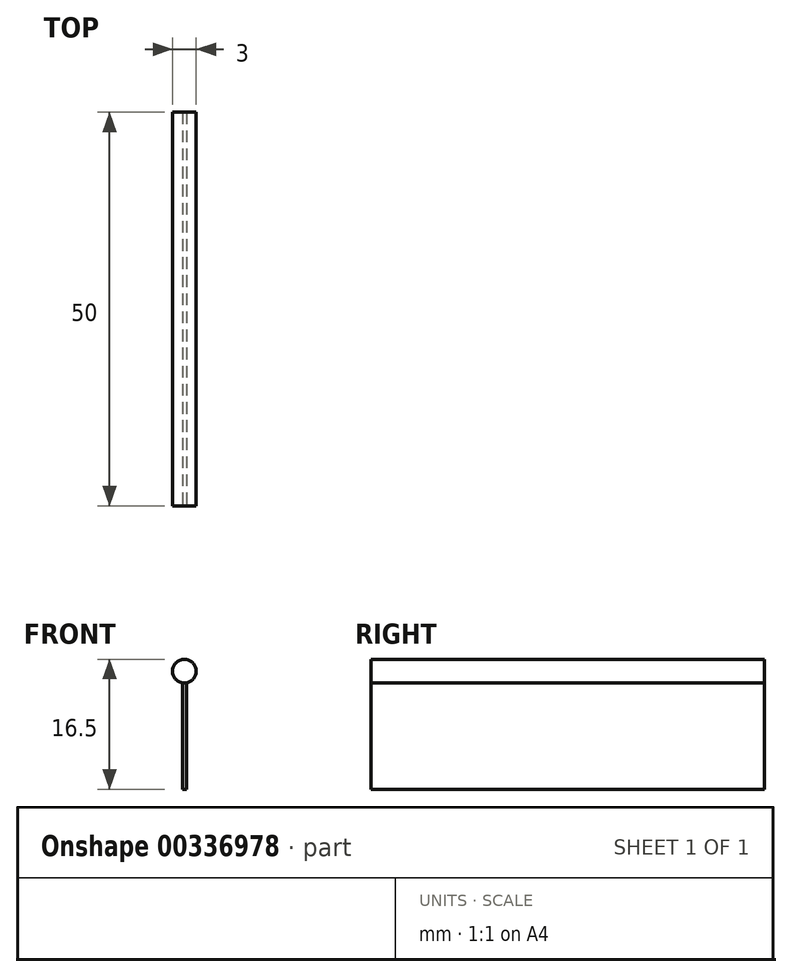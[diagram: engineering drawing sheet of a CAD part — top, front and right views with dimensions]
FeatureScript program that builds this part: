
annotation { "Feature Type Name" : "Feature", "Feature Type Description" : "" }
export const myFeature = defineFeature(function(context is Context, id is Id, definition is map)
    precondition{}
    {
        {
            var Q0;
            Q0=qCreatedBy(makeId("Front.planeOp"),FACE);
            var sketch = newSketch(context, id + "F0", { "sketchPlane" : qUnion([Q0])});
            skCircle(sketch, "E0", {"center": v(0, 35.6) * mm, "radius": 1.5 * mm});
            skPoint(sketch, "E1.start.orphan", {"position": v(-0.25, 35.6) * mm});
            skSolve(sketch);
        }
        {
            var Q0;
            Q0=makeQuery(id+"F0.imprint","IMPRINT",FACE,{"disambiguationData":[TD([[makeQuery(id+"F0.imprint","IMPRINT",EDGE,{"derivedFrom":sQuery(id+"F0.wireOp",EDGE,"E0")}),1.0]])]});
            extrude(context, id + "F1", {"entities" : qUnion([Q0]), "endBound" : BoundingType.SYMMETRIC, "depth" : 50 * mm});
        }
        {
            var Q0;
            Q0=makeQuery(id+"F1.opExtrude","CAP_FACE",FACE,{"disambiguationData":[OSD([sQuery(id+"F0.wireOp",EDGE,"E0")])],"isStart":false});
            var sketch = newSketch(context, id + "F2", { "sketchPlane" : qUnion([Q0])});
            skLineSegment(sketch, "E2", {"start": v(0.25, 34.12) * mm, "end": v(0.25, 20.6) * mm});
            skLineSegment(sketch, "E3", {"start": v(0.25, 20.6) * mm, "end": v(-0.25, 20.6) * mm});
            skLineSegment(sketch, "E4", {"start": v(-0.25, 20.6) * mm, "end": v(-0.25, 34.12) * mm});
            skArc(sketch, "E5", {"start": v(-0.25, 34.12) * mm, "mid": v(0, 34.1) * mm, "end": v(0.25, 34.12) * mm});
            skPoint(sketch, "E6.start.orphan", {"position": v(-0.25, 35.6) * mm});
            skSolve(sketch);
        }
        {
            var Q0;
            Q0=makeQuery(id+"F2.imprint","IMPRINT",FACE,{"disambiguationData":[TD([[makeQuery(id+"F2.imprint","IMPRINT",EDGE,{"derivedFrom":sQuery(id+"F2.wireOp",EDGE,"E2")}),-1.0]])]});
            extrude(context, id + "F3", {"entities" : qUnion([Q0]), "oppositeDirection" : true, "depth" : 50 * mm});
        }
    });
